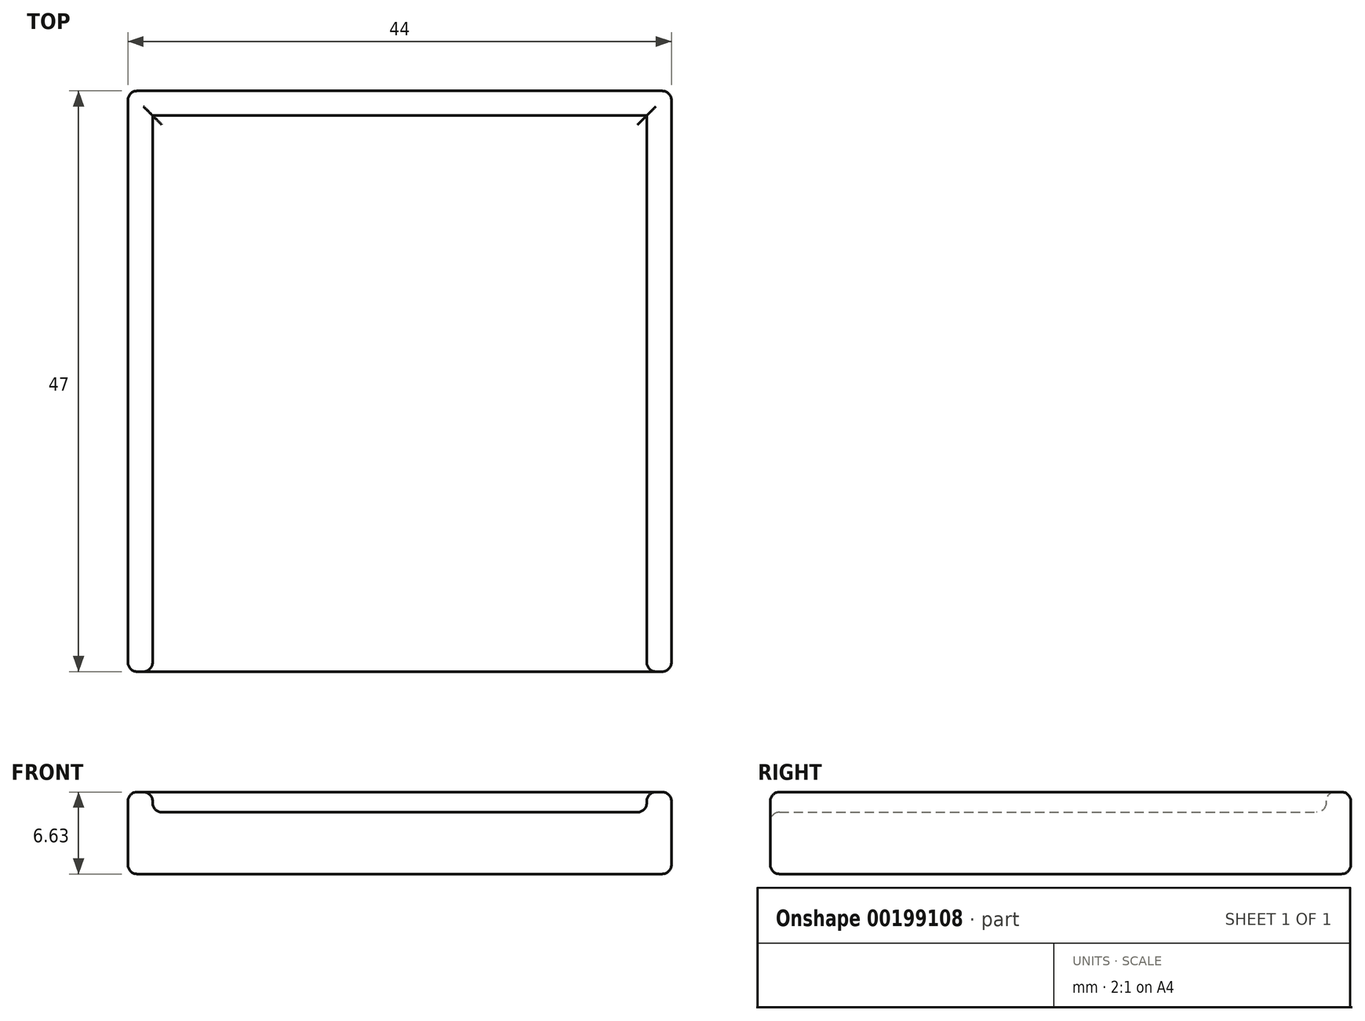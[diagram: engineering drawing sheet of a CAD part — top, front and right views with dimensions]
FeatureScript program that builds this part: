
annotation { "Feature Type Name" : "Feature", "Feature Type Description" : "" }
export const myFeature = defineFeature(function(context is Context, id is Id, definition is map)
    precondition{}
    {
        {
            var Q0;
            Q0=qCreatedBy(makeId("Front.planeOp"),FACE);
            var sketch = newSketch(context, id + "F0", { "sketchPlane" : qUnion([Q0])});
            skLineSegment(sketch, "E0.top", {"start": v(-0.67, -8.13) * mm, "end": v(43.33, -8.13) * mm});
            skLineSegment(sketch, "E0.left", {"start": v(-0.67, -1.5) * mm, "end": v(-0.67, -8.13) * mm});
            skLineSegment(sketch, "E0.right", {"start": v(43.33, -1.5) * mm, "end": v(43.33, -8.13) * mm});
            skLineSegment(sketch, "E1", {"start": v(1.33, -1.5) * mm, "end": v(1.33, -3.13) * mm});
            skLineSegment(sketch, "E2", {"start": v(1.33, -3.13) * mm, "end": v(41.33, -3.13) * mm});
            skLineSegment(sketch, "E3", {"start": v(41.33, -3.13) * mm, "end": v(41.33, -1.5) * mm});
            skLineSegment(sketch, "E4", {"start": v(-0.67, -1.5) * mm, "end": v(1.33, -1.5) * mm});
            skLineSegment(sketch, "E5", {"start": v(41.33, -1.5) * mm, "end": v(43.33, -1.5) * mm});
            skLineSegment(sketch, "E6", {"start": v(1.33, -1.5) * mm, "end": v(41.33, -1.5) * mm});
            skSolve(sketch);
        }
        {
            var Q0;
            Q0=makeQuery(id+"F0.imprint","IMPRINT",FACE,{"disambiguationData":[TD([[makeQuery(id+"F0.imprint","IMPRINT",EDGE,{"derivedFrom":sQuery(id+"F0.wireOp",EDGE,"E0.top")}),1.0]])]});
            extrude(context, id + "F1", {"entities" : qUnion([Q0]), "depth" : 47 * mm});
        }
        {
            var Q0;
            Q0=makeQuery(id+"F0.imprint","IMPRINT",FACE,{"disambiguationData":[TD([[makeQuery(id+"F0.imprint","IMPRINT",EDGE,{"derivedFrom":sQuery(id+"F0.wireOp",EDGE,"E1")}),1.0]])]});
            extrude(context, id + "F2", {"entities" : qUnion([Q0]), "operationType" : NewBodyOperationType.ADD, "depth" : 2 * mm});
        }
        {
            var Q0;
            Q0=makeQuery(id+"F2.boolean.opBoolean","MERGE",FACE,{"derivedFrom":[makeQuery(id+"F1.opExtrude","SWEPT_FACE",FACE,{"disambiguationData":[OSD([sQuery(id+"F0.wireOp",EDGE,"E4")])]}),makeQuery(id+"F1.opExtrude","SWEPT_FACE",FACE,{"disambiguationData":[OSD([sQuery(id+"F0.wireOp",EDGE,"E5")])]}),makeQuery(id+"F2.opExtrude","SWEPT_FACE",FACE,{"disambiguationData":[OSD([sQuery(id+"F0.wireOp",EDGE,"E6")])]})]});
            var Q1;
            Q1=makeQuery(id+"F1.opExtrude","SWEPT_FACE",FACE,{"disambiguationData":[OSD([sQuery(id+"F0.wireOp",EDGE,"E2")])]});
            var Q2;
            Q2=makeQuery(id+"F1.opExtrude","SWEPT_FACE",FACE,{"disambiguationData":[OSD([sQuery(id+"F0.wireOp",EDGE,"E0.top")])]});
            var Q3;
            {var subQ0=sQuery(id+"F0.wireOp",EDGE,"E3");var subQ1=sQuery(id+"F0.wireOp",EDGE,"E2");var subQ2=sQuery(id+"F0.wireOp",EDGE,"E1");Q3=makeQuery(id+"F2.boolean.opBoolean","MERGE",FACE,{"derivedFrom":[makeQuery(id+"F1.opExtrude","CAP_FACE",FACE,{"disambiguationData":[OSD([sQuery(id+"F0.wireOp",EDGE,"E0.top"),sQuery(id+"F0.wireOp",EDGE,"E0.left"),sQuery(id+"F0.wireOp",EDGE,"E0.right"),subQ2,subQ1,subQ0,sQuery(id+"F0.wireOp",EDGE,"E4"),sQuery(id+"F0.wireOp",EDGE,"E5")])],"isStart":true}),makeQuery(id+"F2.opExtrude","CAP_FACE",FACE,{"disambiguationData":[OSD([subQ2,subQ1,subQ0,sQuery(id+"F0.wireOp",EDGE,"E6")])],"isStart":true})]});}
            var Q4;
            Q4=makeQuery(id+"F1.opExtrude","SWEPT_FACE",FACE,{"disambiguationData":[OSD([sQuery(id+"F0.wireOp",EDGE,"E0.left")])]});
            var Q5;
            Q5=makeQuery(id+"F1.opExtrude","CAP_FACE",FACE,{"disambiguationData":[OSD([sQuery(id+"F0.wireOp",EDGE,"E0.top"),sQuery(id+"F0.wireOp",EDGE,"E0.left"),sQuery(id+"F0.wireOp",EDGE,"E0.right"),sQuery(id+"F0.wireOp",EDGE,"E1"),sQuery(id+"F0.wireOp",EDGE,"E2"),sQuery(id+"F0.wireOp",EDGE,"E3"),sQuery(id+"F0.wireOp",EDGE,"E4"),sQuery(id+"F0.wireOp",EDGE,"E5")])],"isStart":false});
            var Q6;
            Q6=makeQuery(id+"F1.opExtrude","SWEPT_EDGE",EDGE,{"disambiguationData":[OSD([sQuery(id+"F0.wireOp",EDGE,"E0.top"),sQuery(id+"F0.wireOp",EDGE,"E0.right")])]});
            fillet(context, id + "F3", {"entities" : qUnion([Q0, Q1, Q2, Q3, Q4, Q5, Q6]), "radius" : 0.75 * mm, "tangentPropagation" : true, "allowEdgeOverflow" : false});
        }
    });
